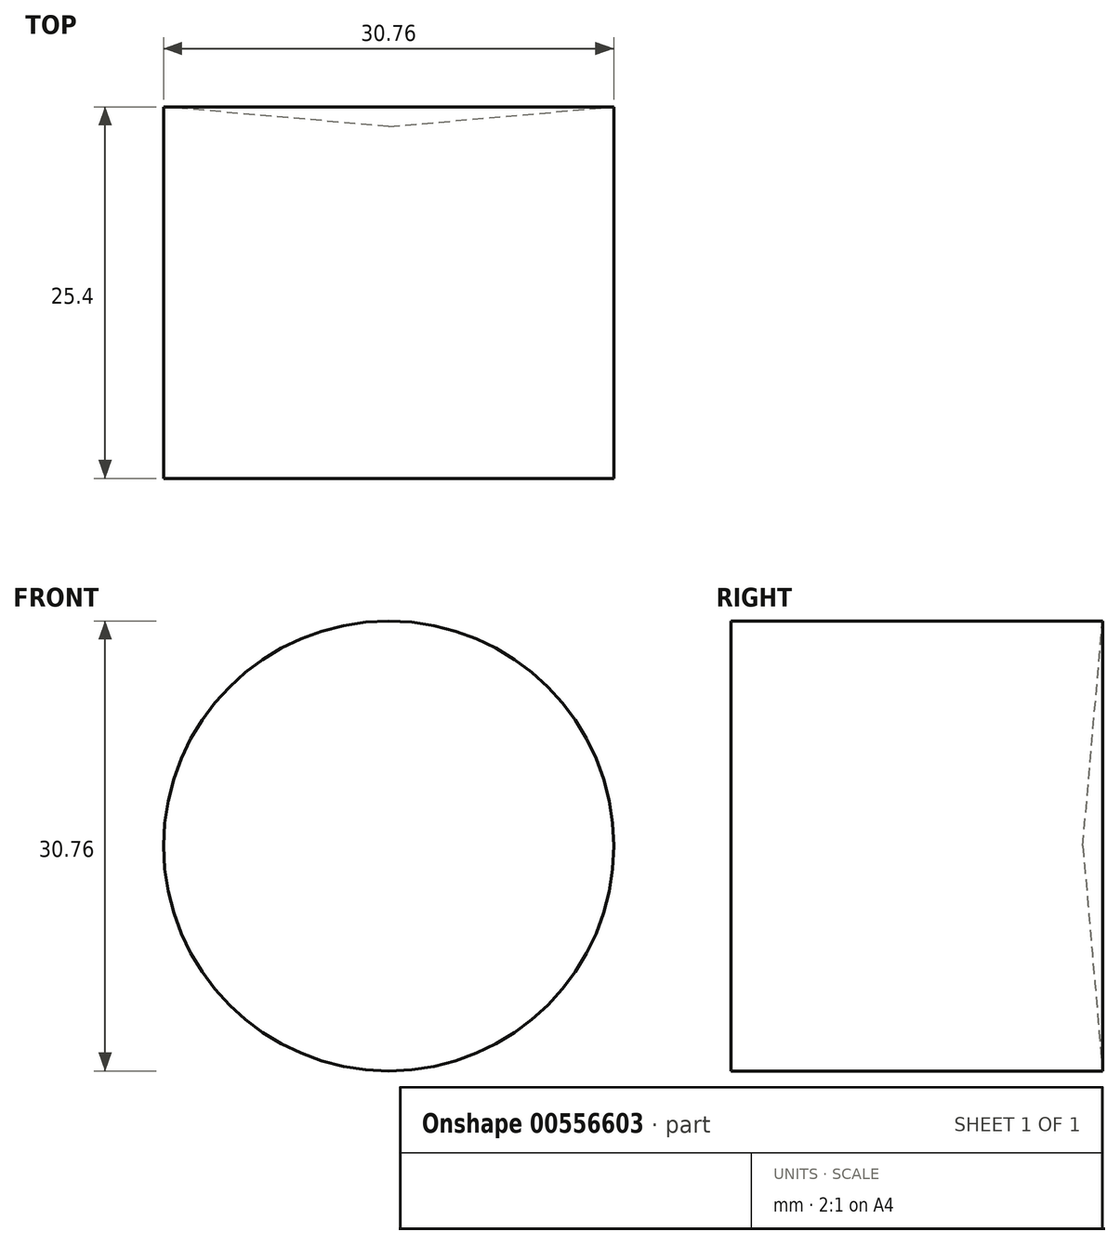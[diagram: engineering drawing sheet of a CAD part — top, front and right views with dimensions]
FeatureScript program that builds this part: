
annotation { "Feature Type Name" : "Feature", "Feature Type Description" : "" }
export const myFeature = defineFeature(function(context is Context, id is Id, definition is map)
    precondition{}
    {
        {
            var Q0;
            Q0=qCreatedBy(makeId("Front.planeOp"),FACE);
            var sketch = newSketch(context, id + "F0", { "sketchPlane" : qUnion([Q0])});
            skCircle(sketch, "E0", {"center": v(0, 0) * mm, "radius": 15.38 * mm});
            skSolve(sketch);
        }
        {
            var Q0;
            Q0 = qSketchRegion(id + "F0", true);
            extrude(context, id + "F1", {"entities" : qUnion([Q0]), "depth" : 25.4 * mm, "offsetDistance" : 25.4 * mm});
        }
        {
            var Q0;
            Q0 = qSketchRegion(id + "F0", true);
            extrude(context, id + "F2", {"entities" : qUnion([Q0]), "operationType" : NewBodyOperationType.REMOVE, "depth" : 8.64 * mm, "offsetDistance" : 25.4 * mm, "hasDraft" : true, "draftAngle" : 85 * degree, "draftPullDirection" : true});
        }
    });
